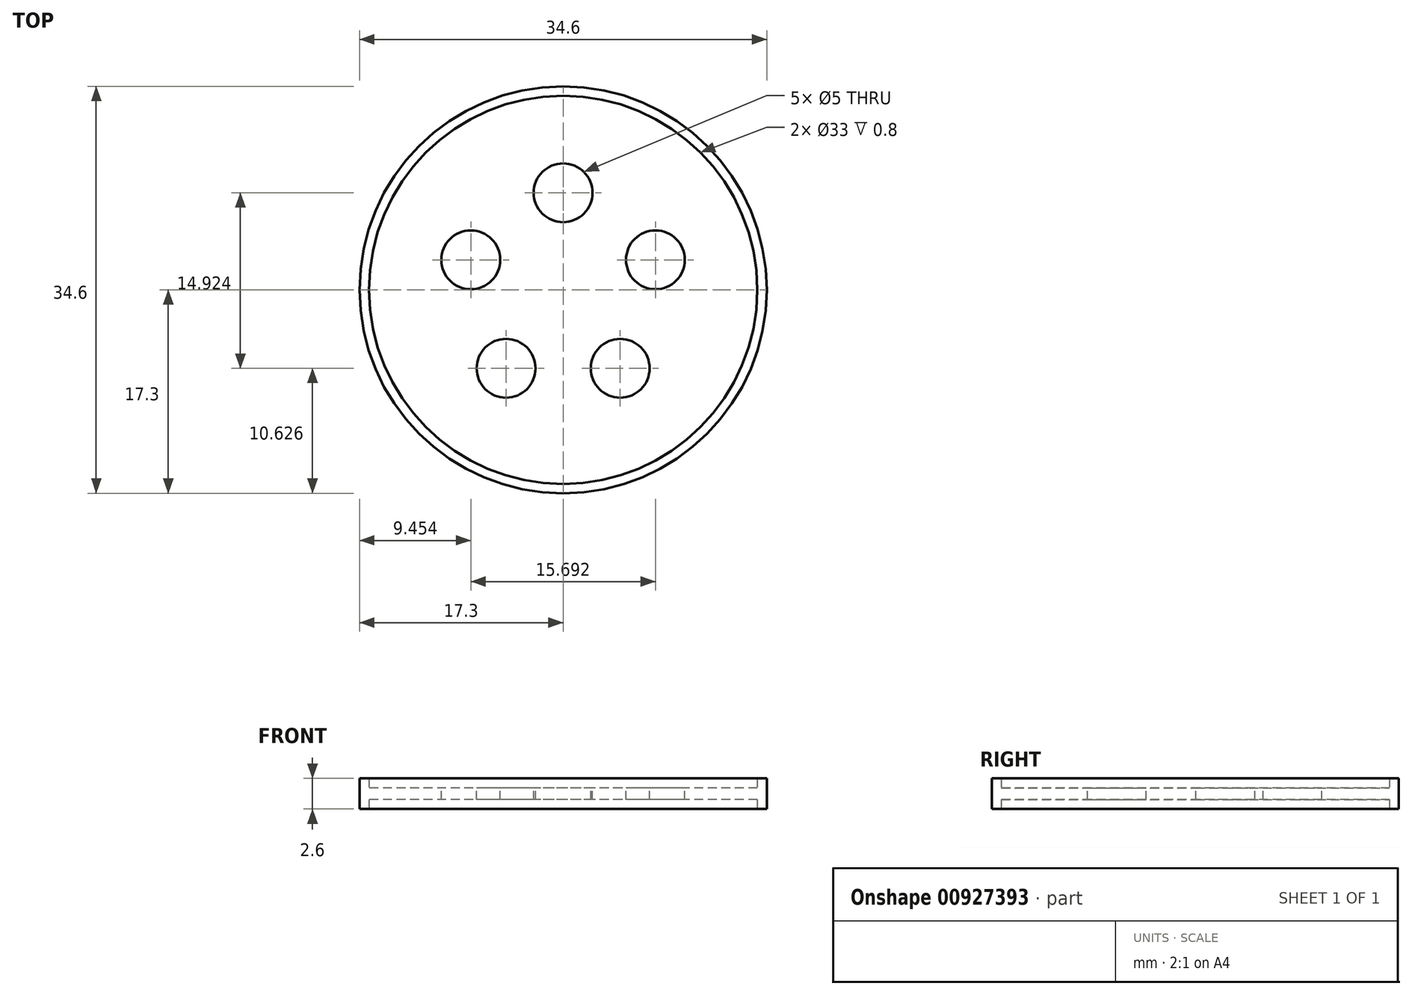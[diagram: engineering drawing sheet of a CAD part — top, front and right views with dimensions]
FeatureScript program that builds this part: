
annotation { "Feature Type Name" : "Feature", "Feature Type Description" : "" }
export const myFeature = defineFeature(function(context is Context, id is Id, definition is map)
    precondition{}
    {
        {
            var Q0;
            Q0=qCreatedBy(makeId("Top.planeOp"),FACE);
            var sketch = newSketch(context, id + "F0", { "sketchPlane" : qUnion([Q0])});
            skCircle(sketch, "E0", {"center": v(0, 0) * mm, "radius": 16.5 * mm});
            skCircle(sketch, "E1", {"center": v(0, 0) * mm, "radius": 17.3 * mm});
            skSolve(sketch);
        }
        {
            var Q0;
            Q0 = qSketchRegion(id + "F0", true);
            extrude(context, id + "F1", {"entities" : qUnion([Q0]), "depth" : 1.3 * mm, "offsetDistance" : 25 * mm, "hasSecondDirection" : true, "secondDirectionOppositeDirection" : true, "secondDirectionDepth" : 1.3 * mm});
        }
        {
            var Q0;
            Q0=qCreatedBy(makeId("Top.planeOp"),FACE);
            var sketch = newSketch(context, id + "F2", { "sketchPlane" : qUnion([Q0])});
            skCircle(sketch, "E2", {"center": v(0, 0) * mm, "radius": 17.25 * mm});
            skSolve(sketch);
        }
        {
            var Q0;
            Q0 = qSketchRegion(id + "F2", true);
            extrude(context, id + "F3", {"entities" : qUnion([Q0]), "operationType" : NewBodyOperationType.ADD, "depth" : 0.5 * mm, "offsetDistance" : 25 * mm, "hasSecondDirection" : true, "secondDirectionOppositeDirection" : true, "secondDirectionDepth" : 0.5 * mm});
        }
        {
            var Q0;
            Q0=qCreatedBy(makeId("Top.planeOp"),FACE);
            var sketch = newSketch(context, id + "F4", { "sketchPlane" : qUnion([Q0])});
            skCircle(sketch, "E3", {"center": v(0, 8.25) * mm, "radius": 2.5 * mm});
            skPoint(sketch, "E4.center", {"position": v(0, 0) * mm});
            skCircle(sketch, "E5.1.0", {"center": v(-7.85, 2.55) * mm, "radius": 2.5 * mm});
            skCircle(sketch, "E5.2.0", {"center": v(-4.85, -6.67) * mm, "radius": 2.5 * mm});
            skCircle(sketch, "E5.3.0", {"center": v(4.85, -6.67) * mm, "radius": 2.5 * mm});
            skCircle(sketch, "E5.4.0", {"center": v(7.85, 2.55) * mm, "radius": 2.5 * mm});
            skSolve(sketch);
        }
        {
            var Q0;
            Q0 = qSketchRegion(id + "F4", true);
            extrude(context, id + "F5", {"entities" : qUnion([Q0]), "operationType" : NewBodyOperationType.REMOVE, "oppositeDirection" : true, "depth" : 1 * mm, "offsetDistance" : 25 * mm, "hasSecondDirection" : true, "secondDirectionOppositeDirection" : false, "secondDirectionDepth" : 1 * mm});
        }
    });
